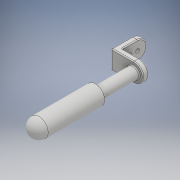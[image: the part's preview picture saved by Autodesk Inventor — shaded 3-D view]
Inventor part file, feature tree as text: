
AUTODESK INVENTOR PART (.ipt)
format: ipt  version: 2018 (Build 220112000, 112)  size: 201,728 bytes
history: native  units: mm
features: extrude x5, sketch x5, fillet x4
ambient origin geometry x8: Origin, YZ Plane, XZ Plane, XY Plane, X Axis, Y Axis, Z Axis, Center Point
bodies: Solid1 (feature_tree)
feature tree (14):
  extrude  "Extrusion1"  Depth=10.0mm
  fillet  "Fillet1"  Radius=3.0mm
  extrude  "Extrusion4"  Depth=5.0mm
  extrude  "Extrusion5"  TaperAngle=0.0deg  [1 undecoded]
  fillet  "Fillet2"  Radius=20.0mm
  extrude  "Extrusion6"  Depth=5.0mm TaperAngle=0.0deg
  fillet  "Fillet4"  Radius=5.0mm
  extrude  "Extrusion7"  Depth=10.0mm
  fillet  "Fillet5"  Radius=13.0mm
  sketch  "Sketch2"  dims[d2=17.0mm d3=10.0mm d5=3.0mm d6=0.0mm]
  sketch  "Sketch5"  dims[d10=5.0mm d19=6.0mm]
  sketch  "Sketch6"  dims[d20=5.0mm d21=0.0mm d22=20.0mm d23=0.0mm]
  sketch  "Sketch7"  dims[d24=10.0mm d25=35.6mm d26=0.0mm d27=5.0mm]
  sketch  "Sketch8"  dims[d29=3.0mm d30=10.0mm d31=13.0mm d32=0.0mm d33=5.0mm d34=2.0mm d35=2.0mm d36=0.0mm d37=4.0mm d38=5.0mm d39=5.0mm d40=10.0mm d41=5.0mm d42=3.0mm d43=0.0mm d44=0.5mm]
note: 1 required parameter value undecoded (feature->parameter linkage not recoverable at this tier; creation-order binding heuristic only, values carry confidence <= 0.55)
